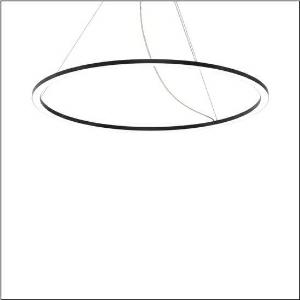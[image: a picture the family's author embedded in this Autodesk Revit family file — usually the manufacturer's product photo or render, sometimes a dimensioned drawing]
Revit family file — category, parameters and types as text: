
# Revit family: silica_r__21_ring-d_5pjbd4d1104a_1e9f
name_source: partatom
category: Lighting Fixtures
units: mm (PartAtom-declared; Revit-internal decimal feet)

## family parameters
Cut with Voids When Loaded = No
Host = Face
Light Source = No
Part Type = Normal
Room Calculation Point = No
Round Connector Dimension = Use Diameter
Shared = No

## types (1)
- Silica® 21 Ring-D (1 x LED, 10840 lm, 125 W, 3000K)
    Apparent Load = 125 VA
    CIE Flux Codes = 37 69 92 100 100
    Color Rendering = 80
    Color Temperature = 3000K
    Default Elevation = 1800 mm
    Description = Silica® 21 Ring-D, suspended luminaire, of PMMA, frosted, light emission: ring underside luminous distribution, primary light characteristic: symmetric, installation type: suspended mounting, LED, rated luminous flux: 10.840lm, luminous efficacy: 87lm/W, light colour: 830, colour temperature: 3000K, control gear: DALI 2, with terminal, 5-pole, mains connection: 230V, AC/DC, 0/50..60Hz, rated input power: 125W, housing, of extruded aluminium section, jet black (RAL 9005), diameter: 1.450mm, ceiling canopy, jet black (RAL 9005), protection rating (lamp compartment): IP40, insulation class (complete): insulation class I (protective earthing), certification: CE, impact resistance: IK02, permissible operating ambient temperature: 0..+35°C, packaging unit: 1 piece
    Height = 25 mm  [stored 0.082021 ft]
    Lamp = 1 x LED
    Lamp Light Flux = 10840 lm
    Lamp Power = 125 W
    Lamp count = 1
    Length = 1450 mm
    Luminous efficacy = 87 lm/W
    Manufacturer = Siteco
    ModVariant = No
    Model = 5PJBD4D1104A
    Mounting Place = Ceiling
    Mounting Type = Pendant
    Number of Poles = 1
    OnlyDefault = Yes
    Power Factor = 1
    Product Name = Silica® 21 Ring-D
    Product group = suspended luminaire
    ProductGroupID = 904
    Protection Class = Protection class I
    Protection Degree = IP 40
    RLX_Detail_Level = 1
    RLX_Emergency_Light_Flux = 0 lm
    RLX_Emergency_Type = 0
    RLX_Emergency_Type_DB = No
    RlxData = <blob elided: 19401 chars, md5=2784604b>
    Socket = socket
    Standby Power = 0 W
    System Light Flux = 10840 lm
    System Power = 125 W
    Type Comments = Product without accessories
    Type Image = l_1258357.jpg
    URL = http://relux.com
    VarID = ---
    Voltage = 0 V
    Weight = 0.00 kg
    Width = 0 mm  [stored 0 ft]

note: [stored X ft] marks values corroborated as IEEE doubles in the binary element streams (Revit-internal decimal feet)

## geometry (parser evidence)
native form markers: Blend x4, Sweep x11
no freeform markers — native parametric forms only
